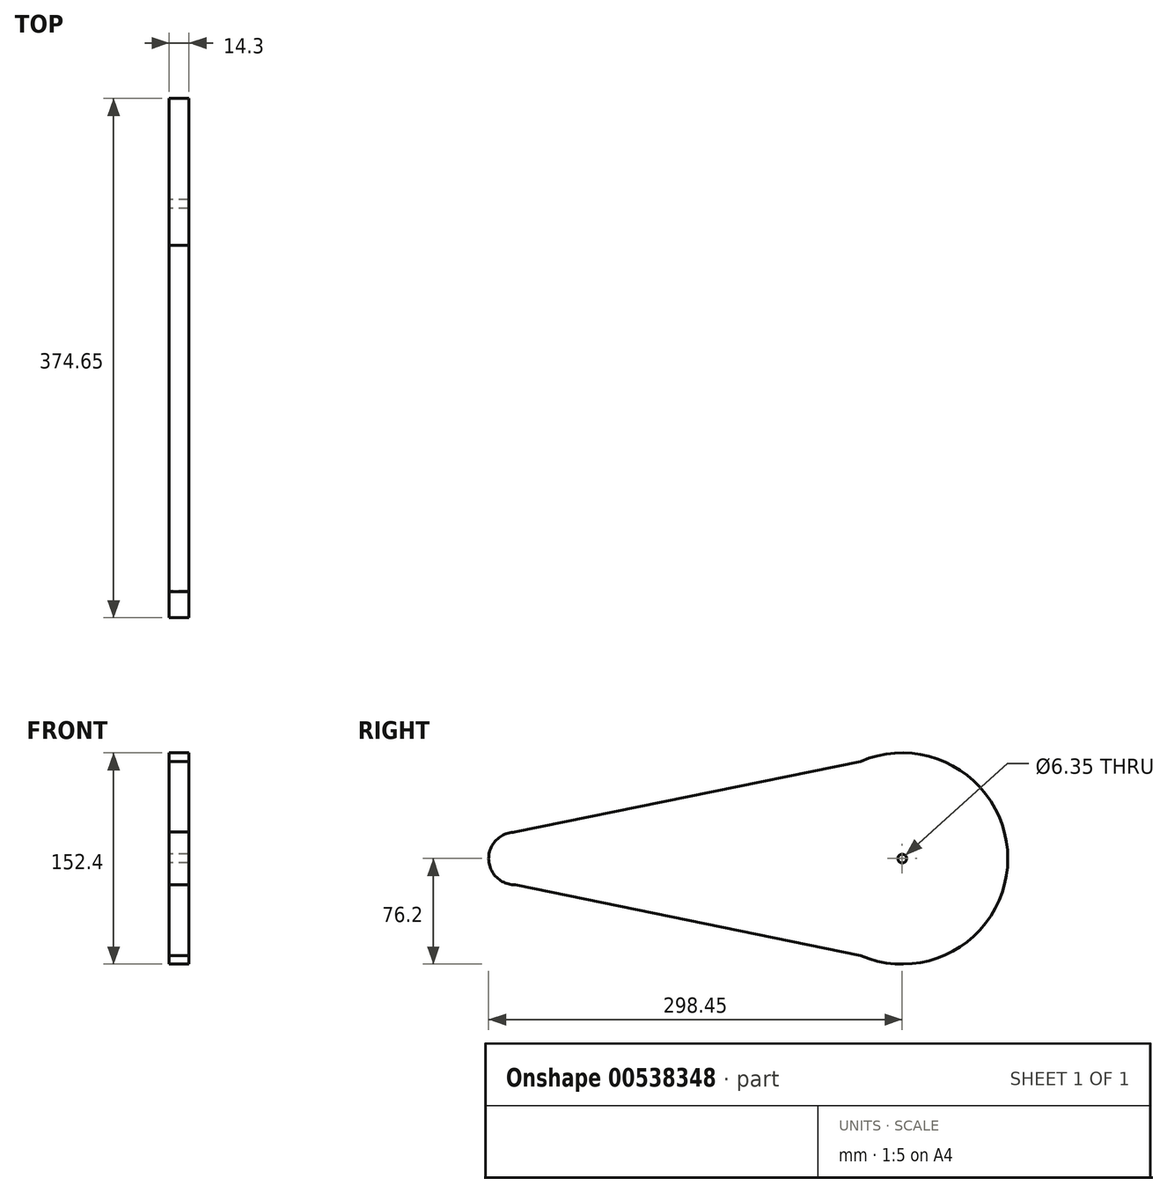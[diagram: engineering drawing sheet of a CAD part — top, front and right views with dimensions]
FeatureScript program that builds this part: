
annotation { "Feature Type Name" : "Feature", "Feature Type Description" : "" }
export const myFeature = defineFeature(function(context is Context, id is Id, definition is map)
    precondition{}
    {
        {
            var Q0;
            Q0=qCreatedBy(makeId("Right.planeOp"),FACE);
            var sketch = newSketch(context, id + "F0", { "sketchPlane" : qUnion([Q0])});
            skCircle(sketch, "E0", {"center": v(0, 0) * mm, "radius": 76.2 * mm});
            skLineSegment(sketch, "E1", {"start": v(0, 0) * mm, "end": v(-279.4, 0) * mm});
            skCircle(sketch, "E2", {"center": v(-279.4, 0) * mm, "radius": 19.05 * mm});
            skCircle(sketch, "E3", {"center": v(0, 0) * mm, "radius": 3.17 * mm});
            skLineSegment(sketch, "E4", {"start": v(0, 76.2) * mm, "end": v(-279.58, 19.05) * mm});
            skLineSegment(sketch, "E5", {"start": v(0, -76.2) * mm, "end": v(-279.14, -19.05) * mm});
            skSolve(sketch);
        }
        {
            var Q0;
            Q0 = qSketchRegion(id + "F0", true);
            extrude(context, id + "F1", {"entities" : qUnion([Q0]), "endBound" : BoundingType.SYMMETRIC, "depth" : 14.3 * mm, "offsetDistance" : 25.4 * mm});
        }
    });
